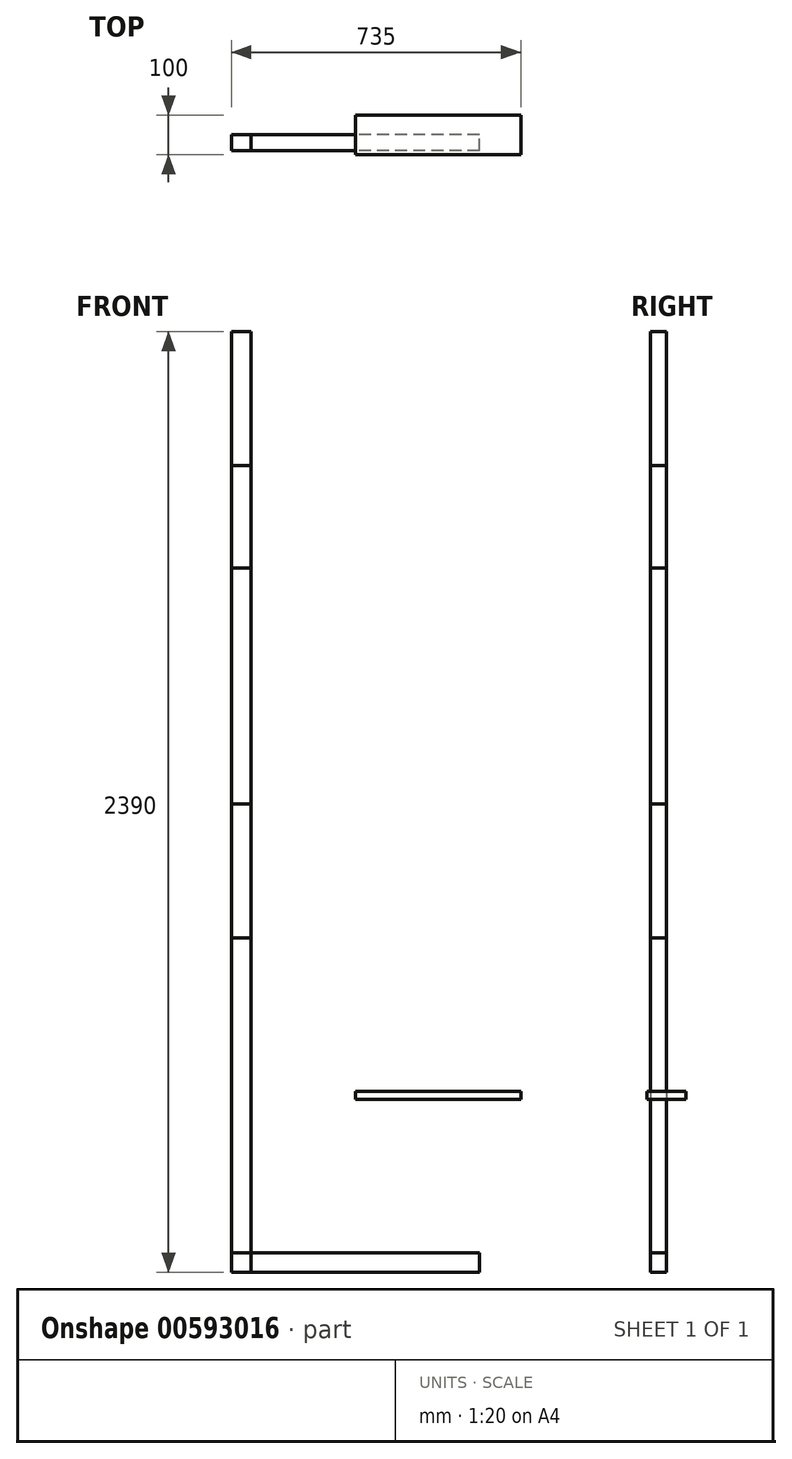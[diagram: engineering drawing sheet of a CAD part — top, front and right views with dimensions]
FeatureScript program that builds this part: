
annotation { "Feature Type Name" : "Feature", "Feature Type Description" : "" }
export const myFeature = defineFeature(function(context is Context, id is Id, definition is map)
    precondition{}
    {
        {
            var Q0;
            Q0=qCreatedBy(makeId("Front.planeOp"),FACE);
            var sketch = newSketch(context, id + "F0", { "sketchPlane" : qUnion([Q0])});
            skLineSegment(sketch, "E0.bottom", {"start": v(265, 400) * mm, "end": v(-265, 400) * mm, "construction": true});
            skLineSegment(sketch, "E0.top", {"start": v(265, -400) * mm, "end": v(-265, -400) * mm});
            skLineSegment(sketch, "E0.left", {"start": v(265, 400) * mm, "end": v(265, -400) * mm, "construction": true});
            skLineSegment(sketch, "E0.right", {"start": v(-265, 400) * mm, "end": v(-265, -400) * mm});
            skPoint(sketch, "E0.middle", {"position": v(0, 0) * mm});
            skLineSegment(sketch, "E1.0", {"start": v(315, -450) * mm, "end": v(-315, -450) * mm});
            skLineSegment(sketch, "E1.1", {"start": v(-315, 400) * mm, "end": v(-315, -450) * mm});
            skLineSegment(sketch, "E2", {"start": v(-315, 400) * mm, "end": v(-265, 400) * mm});
            skLineSegment(sketch, "E3", {"start": v(265, -400) * mm, "end": v(315, -450) * mm, "construction": true});
            skLineSegment(sketch, "E4", {"start": v(-265, -400) * mm, "end": v(-315, -400) * mm});
            skLineSegment(sketch, "E5", {"start": v(-265, -400) * mm, "end": v(-265, -450) * mm});
            skLineSegment(sketch, "E6", {"start": v(265, -400) * mm, "end": v(315, -400) * mm});
            skLineSegment(sketch, "E7", {"start": v(315, -400) * mm, "end": v(315, -450) * mm});
            skSolve(sketch);
        }
        {
            var Q0;
            Q0=makeQuery(id+"F0.imprint","IMPRINT",FACE,{"disambiguationData":[TD([[makeQuery(id+"F0.imprint","IMPRINT",EDGE,{"derivedFrom":sQuery(id+"F0.wireOp",EDGE,"E0.right")}),-1.0]])]});
            var Q1;
            {var subQ4=sQuery(id+"F0.wireOp",EDGE,"E4");Q1=makeQuery(id+"F0.imprint","IMPRINT",FACE,{"disambiguationData":[TD([[makeQuery(id+"F0.imprint","IMPRINT",EDGE,{"derivedFrom":subQ4}),1.0]])]});}
            extrude(context, id + "F1", {"entities" : qUnion([Q0, Q1]), "depth" : 40 * mm, "offsetDistance" : 25 * mm});
        }
        {
            var Q0;
            Q0=makeQuery(id+"F0.imprint","IMPRINT",FACE,{"disambiguationData":[TD([[makeQuery(id+"F0.imprint","IMPRINT",EDGE,{"derivedFrom":sQuery(id+"F0.wireOp",EDGE,"E0.top")}),1.0]])]});
            var Q1;
            {var subQ4=sQuery(id+"F0.wireOp",EDGE,"E4");Q1=makeQuery(id+"F0.imprint","IMPRINT",FACE,{"disambiguationData":[TD([[makeQuery(id+"F0.imprint","IMPRINT",EDGE,{"derivedFrom":subQ4}),1.0]])]});}
            extrude(context, id + "F2", {"entities" : qUnion([Q0, Q1]), "depth" : 40 * mm, "offsetDistance" : 25 * mm});
        }
        {
            var Q0;
            Q0=makeQuery(id+"F1.opExtrude","SWEPT_FACE",FACE,{"disambiguationData":[OSD([sQuery(id+"F0.wireOp",EDGE,"E2")])]});
            extrude(context, id + "F3", {"entities" : qUnion([Q0]), "depth" : 340 * mm, "offsetDistance" : 25 * mm});
        }
        {
            var Q0;
            Q0=makeQuery(id+"F3.opExtrude","CAP_FACE",FACE,{"disambiguationData":[OSD([sQuery(id+"F0.wireOp",EDGE,"E2")])],"isStart":false});
            extrude(context, id + "F4", {"entities" : qUnion([Q0]), "depth" : 600 * mm, "offsetDistance" : 25 * mm});
        }
        {
            var Q0;
            Q0=makeQuery(id+"F4.opExtrude","CAP_FACE",FACE,{"disambiguationData":[OSD([sQuery(id+"F0.wireOp",EDGE,"E2")])],"isStart":false});
            extrude(context, id + "F5", {"entities" : qUnion([Q0]), "depth" : 260 * mm, "offsetDistance" : 25 * mm});
        }
        {
            var Q0;
            Q0=makeQuery(id+"F5.opExtrude","CAP_FACE",FACE,{"disambiguationData":[OSD([sQuery(id+"F0.wireOp",EDGE,"E2")])],"isStart":false});
            extrude(context, id + "F6", {"entities" : qUnion([Q0]), "depth" : (260 + 50 + 30) * mm, "offsetDistance" : 25 * mm});
        }
        {
            var Q0;
            Q0=qCreatedBy(makeId("Right.planeOp"),FACE);
            var sketch = newSketch(context, id + "F7", { "sketchPlane" : qUnion([Q0])});
            skLineSegment(sketch, "E8.bottom", {"start": v(50, 10) * mm, "end": v(-50, 10) * mm});
            skLineSegment(sketch, "E8.top", {"start": v(50, -10) * mm, "end": v(-50, -10) * mm});
            skLineSegment(sketch, "E8.left", {"start": v(50, 10) * mm, "end": v(50, -10) * mm});
            skLineSegment(sketch, "E8.right", {"start": v(-50, 10) * mm, "end": v(-50, -10) * mm});
            skPoint(sketch, "E8.middle", {"position": v(0, 0) * mm});
            skSolve(sketch);
        }
        {
            var Q0;
            Q0 = qSketchRegion(id + "F7", true);
            extrude(context, id + "F8", {"entities" : qUnion([Q0]), "depth" : 420 * mm, "offsetDistance" : 25 * mm});
        }
    });
